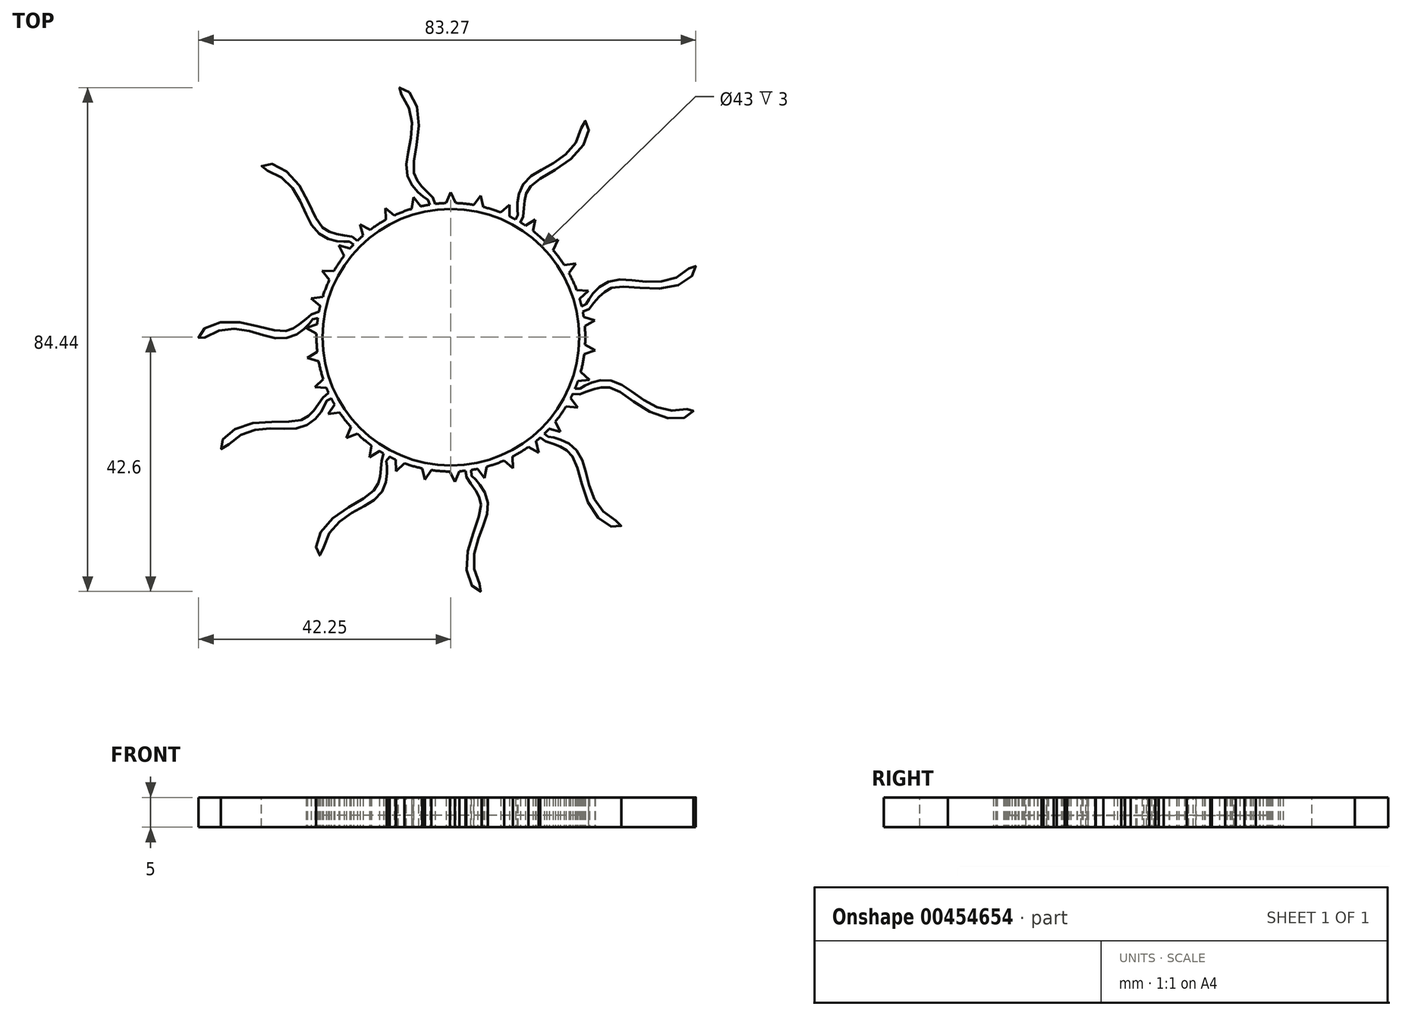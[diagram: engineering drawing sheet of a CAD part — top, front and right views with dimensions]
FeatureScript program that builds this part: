
annotation { "Feature Type Name" : "Feature", "Feature Type Description" : "" }
export const myFeature = defineFeature(function(context is Context, id is Id, definition is map)
    precondition{}
    {
        {
            var Q0;
            Q0=qCreatedBy(makeId("Top.planeOp"),FACE);
            var sketch = newSketch(context, id + "F0", { "sketchPlane" : qUnion([Q0])});
            skCircle(sketch, "E0", {"center": v(0, 0) * mm, "radius": 22.5 * mm});
            skLineSegment(sketch, "E1", {"start": v(-0.8, 22.49) * mm, "end": v(0, 24.26) * mm});
            skLineSegment(sketch, "E2", {"start": v(0, 24.26) * mm, "end": v(0.8, 22.49) * mm});
            skLineSegment(sketch, "E3.1.0", {"start": v(5, 23.74) * mm, "end": v(5.41, 21.84) * mm});
            skLineSegment(sketch, "E3.1.1", {"start": v(3.86, 22.17) * mm, "end": v(5, 23.74) * mm});
            skLineSegment(sketch, "E3.2.0", {"start": v(9.79, 22.2) * mm, "end": v(9.8, 20.25) * mm});
            skLineSegment(sketch, "E3.2.1", {"start": v(8.35, 20.9) * mm, "end": v(9.79, 22.2) * mm});
            skLineSegment(sketch, "E3.3.0", {"start": v(14.16, 19.7) * mm, "end": v(13.76, 17.8) * mm});
            skLineSegment(sketch, "E3.3.1", {"start": v(12.47, 18.73) * mm, "end": v(14.16, 19.7) * mm});
            skLineSegment(sketch, "E3.4.0", {"start": v(17.91, 16.37) * mm, "end": v(17.14, 14.58) * mm});
            skLineSegment(sketch, "E3.4.1", {"start": v(16.07, 15.75) * mm, "end": v(17.91, 16.37) * mm});
            skLineSegment(sketch, "E3.5.0", {"start": v(20.9, 12.32) * mm, "end": v(19.77, 10.73) * mm});
            skLineSegment(sketch, "E3.5.1", {"start": v(18.97, 12.1) * mm, "end": v(20.9, 12.32) * mm});
            skLineSegment(sketch, "E3.6.0", {"start": v(23, 7.75) * mm, "end": v(21.56, 6.43) * mm});
            skLineSegment(sketch, "E3.6.1", {"start": v(21.06, 7.93) * mm, "end": v(23, 7.75) * mm});
            skLineSegment(sketch, "E3.7.0", {"start": v(24.1, 2.84) * mm, "end": v(22.42, 1.85) * mm});
            skLineSegment(sketch, "E3.7.1", {"start": v(22.24, 3.42) * mm, "end": v(24.1, 2.84) * mm});
            skLineSegment(sketch, "E3.8.0", {"start": v(24.17, -2.19) * mm, "end": v(22.32, -2.82) * mm});
            skLineSegment(sketch, "E3.8.1", {"start": v(22.47, -1.24) * mm, "end": v(24.17, -2.19) * mm});
            skLineSegment(sketch, "E3.9.0", {"start": v(23.2, -7.12) * mm, "end": v(21.26, -7.36) * mm});
            skLineSegment(sketch, "E3.9.1", {"start": v(21.73, -5.84) * mm, "end": v(23.2, -7.12) * mm});
            skLineSegment(sketch, "E3.10.0", {"start": v(21.23, -11.75) * mm, "end": v(19.29, -11.58) * mm});
            skLineSegment(sketch, "E3.10.1", {"start": v(20.06, -10.2) * mm, "end": v(21.23, -11.75) * mm});
            skLineSegment(sketch, "E3.11.0", {"start": v(18.35, -15.87) * mm, "end": v(16.49, -15.31) * mm});
            skLineSegment(sketch, "E3.11.1", {"start": v(17.52, -14.11) * mm, "end": v(18.35, -15.87) * mm});
            skLineSegment(sketch, "E3.12.0", {"start": v(14.68, -19.32) * mm, "end": v(12.98, -18.38) * mm});
            skLineSegment(sketch, "E3.12.1", {"start": v(14.24, -17.42) * mm, "end": v(14.68, -19.32) * mm});
            skLineSegment(sketch, "E3.13.0", {"start": v(10.39, -21.93) * mm, "end": v(8.9, -20.66) * mm});
            skLineSegment(sketch, "E3.13.1", {"start": v(10.34, -19.98) * mm, "end": v(10.39, -21.93) * mm});
            skLineSegment(sketch, "E3.14.0", {"start": v(5.64, -23.6) * mm, "end": v(4.46, -22.05) * mm});
            skLineSegment(sketch, "E3.14.1", {"start": v(6, -21.68) * mm, "end": v(5.64, -23.6) * mm});
            skLineSegment(sketch, "E3.15.0", {"start": v(0.66, -24.26) * mm, "end": v(-0.18, -22.5) * mm});
            skLineSegment(sketch, "E3.15.1", {"start": v(1.4, -22.46) * mm, "end": v(0.66, -24.26) * mm});
            skLineSegment(sketch, "E3.16.0", {"start": v(-4.36, -23.87) * mm, "end": v(-4.82, -21.98) * mm});
            skLineSegment(sketch, "E3.16.1", {"start": v(-3.26, -22.26) * mm, "end": v(-4.36, -23.87) * mm});
            skLineSegment(sketch, "E3.17.0", {"start": v(-9.18, -22.46) * mm, "end": v(-9.25, -20.51) * mm});
            skLineSegment(sketch, "E3.17.1", {"start": v(-7.78, -21.11) * mm, "end": v(-9.18, -22.46) * mm});
            skLineSegment(sketch, "E3.18.0", {"start": v(-13.62, -20.08) * mm, "end": v(-13.28, -18.17) * mm});
            skLineSegment(sketch, "E3.18.1", {"start": v(-11.96, -19.06) * mm, "end": v(-13.62, -20.08) * mm});
            skLineSegment(sketch, "E3.19.0", {"start": v(-17.46, -16.84) * mm, "end": v(-16.74, -15.04) * mm});
            skLineSegment(sketch, "E3.19.1", {"start": v(-15.63, -16.18) * mm, "end": v(-17.46, -16.84) * mm});
            skLineSegment(sketch, "E3.20.0", {"start": v(-20.56, -12.88) * mm, "end": v(-19.48, -11.27) * mm});
            skLineSegment(sketch, "E3.20.1", {"start": v(-18.63, -12.61) * mm, "end": v(-20.56, -12.88) * mm});
            skLineSegment(sketch, "E3.21.0", {"start": v(-22.78, -8.37) * mm, "end": v(-21.38, -7) * mm});
            skLineSegment(sketch, "E3.21.1", {"start": v(-20.83, -8.5) * mm, "end": v(-22.78, -8.37) * mm});
            skLineSegment(sketch, "E3.22.0", {"start": v(-24.01, -3.5) * mm, "end": v(-22.37, -2.45) * mm});
            skLineSegment(sketch, "E3.22.1", {"start": v(-22.14, -4.02) * mm, "end": v(-24.01, -3.5) * mm});
            skLineSegment(sketch, "E3.23.0", {"start": v(-24.22, 1.53) * mm, "end": v(-22.4, 2.21) * mm});
            skLineSegment(sketch, "E3.23.1", {"start": v(-22.5, 0.63) * mm, "end": v(-24.22, 1.53) * mm});
            skLineSegment(sketch, "E3.24.0", {"start": v(-23.38, 6.5) * mm, "end": v(-21.45, 6.78) * mm});
            skLineSegment(sketch, "E3.24.1", {"start": v(-21.88, 5.25) * mm, "end": v(-23.38, 6.5) * mm});
            skLineSegment(sketch, "E3.25.0", {"start": v(-21.54, 11.17) * mm, "end": v(-19.6, 11.06) * mm});
            skLineSegment(sketch, "E3.25.1", {"start": v(-20.33, 9.65) * mm, "end": v(-21.54, 11.17) * mm});
            skLineSegment(sketch, "E3.26.0", {"start": v(-18.77, 15.37) * mm, "end": v(-16.9, 14.86) * mm});
            skLineSegment(sketch, "E3.26.1", {"start": v(-17.9, 13.63) * mm, "end": v(-18.77, 15.37) * mm});
            skLineSegment(sketch, "E3.27.0", {"start": v(-15.2, 18.91) * mm, "end": v(-13.47, 18.02) * mm});
            skLineSegment(sketch, "E3.27.1", {"start": v(-14.7, 17.03) * mm, "end": v(-15.2, 18.91) * mm});
            skLineSegment(sketch, "E3.28.0", {"start": v(-10.98, 21.64) * mm, "end": v(-9.46, 20.41) * mm});
            skLineSegment(sketch, "E3.28.1", {"start": v(-10.88, 19.7) * mm, "end": v(-10.98, 21.64) * mm});
            skLineSegment(sketch, "E3.29.0", {"start": v(-6.28, 23.44) * mm, "end": v(-5.05, 21.93) * mm});
            skLineSegment(sketch, "E3.29.1", {"start": v(-6.59, 21.51) * mm, "end": v(-6.28, 23.44) * mm});
            skLineSegment(sketch, "E3.anchor1", {"start": v(0, 0) * mm, "end": v(-0.8, 22.49) * mm, "construction": true});
            skLineSegment(sketch, "E3.anchor2", {"start": v(0, 0) * mm, "end": v(-6.59, 21.51) * mm, "construction": true});
            skFitSpline(sketch, "E4", {"points": [v(-3.54, 22.22) * mm, v(-3.66, 22.83) * mm, v(-3.97, 23.08) * mm, v(-4.5, 23.46) * mm, v(-5.02, 23.84) * mm, v(-5.92, 24.74) * mm, v(-6.9, 26.1) * mm, v(-7.47, 28.4) * mm, v(-7.12, 31.1) * mm, v(-6.52, 35.07) * mm, v(-7.42, 39.32) * mm, v(-8.79, 41.68) * mm, v(-7.6, 41.59) * mm, v(-5.44, 37.44) * mm, v(-6, 30.78) * mm, v(-6.2, 27.57) * mm, v(-5.72, 26.39) * mm, v(-5.12, 25.54) * mm, v(-4.42, 24.8) * mm, v(-3.37, 23.79) * mm, v(-2.87, 23.19) * mm, v(-2.64, 22.34) * mm], "startDerivative": vector(-2.08, 18.4) * mm, "endDerivative": vector(3.18, -21.05) * mm});
            skCircle(sketch, "E5", {"center": v(0, 0) * mm, "radius": 21.5 * mm});
            skFitSpline(sketch, "E6", {"points": [v(10.83, 19.72) * mm, v(11.22, 20.2) * mm, v(11.22, 20.6) * mm, v(11.17, 21.25) * mm, v(11.12, 21.9) * mm, v(11.23, 23.17) * mm, v(11.65, 24.8) * mm, v(13.03, 26.7) * mm, v(15.33, 28.17) * mm, v(18.76, 30.27) * mm, v(21.44, 33.69) * mm, v(22.37, 36.25) * mm, v(23.06, 35.29) * mm, v(21.27, 30.95) * mm, v(15.8, 27.1) * mm, v(13.22, 25.19) * mm, v(12.62, 24.07) * mm, v(12.36, 23.06) * mm, v(12.24, 22.05) * mm, v(12.14, 20.6) * mm, v(12, 19.83) * mm, v(11.5, 19.11) * mm], "startDerivative": vector(12.75, 13.42) * mm, "endDerivative": vector(-14.08, -15.97) * mm});
            skFitSpline(sketch, "E7", {"points": [v(-16.27, 15.54) * mm, v(-16.72, 15.97) * mm, v(-17.12, 16) * mm, v(-17.76, 16) * mm, v(-18.42, 16.02) * mm, v(-19.67, 16.24) * mm, v(-21.25, 16.8) * mm, v(-23.04, 18.34) * mm, v(-24.3, 20.75) * mm, v(-26.09, 24.36) * mm, v(-29.26, 27.33) * mm, v(-31.73, 28.47) * mm, v(-30.71, 29.07) * mm, v(-26.55, 26.92) * mm, v(-23.2, 21.14) * mm, v(-21.51, 18.4) * mm, v(-20.45, 17.7) * mm, v(-19.47, 17.35) * mm, v(-18.47, 17.14) * mm, v(-17.03, 16.92) * mm, v(-16.28, 16.72) * mm, v(-15.6, 16.16) * mm], "startDerivative": vector(-12.26, 13.87) * mm, "endDerivative": vector(14.68, -15.42) * mm});
            skFitSpline(sketch, "E8", {"points": [v(-22.27, 3.18) * mm, v(-22.9, 3.11) * mm, v(-23.22, 2.9) * mm, v(-23.58, 2.47) * mm, v(-24.08, 1.88) * mm, v(-25, 1.03) * mm, v(-26.44, 0.17) * mm, v(-28.77, -0.2) * mm, v(-31.43, 0.39) * mm, v(-35.34, 1.33) * mm, v(-39.65, 0.8) * mm, v(-42.12, -0.35) * mm, v(-41.92, 0.82) * mm, v(-37.6, 2.62) * mm, v(-31.01, 1.47) * mm, v(-27.83, 1) * mm, v(-26.62, 1.37) * mm, v(-25.72, 1.9) * mm, v(-24.91, 2.53) * mm, v(-23.82, 3.49) * mm, v(-23.18, 3.93) * mm, v(-22.08, 4.3) * mm], "startDerivative": vector(-18.5, -0.47) * mm, "endDerivative": vector(21.25, 1.33) * mm});
            skFitSpline(sketch, "E9", {"points": [v(21.9, 5.19) * mm, v(22.5, 5.35) * mm, v(22.72, 5.68) * mm, v(23.05, 6.23) * mm, v(23.38, 6.8) * mm, v(24.2, 7.77) * mm, v(25.47, 8.86) * mm, v(27.7, 9.63) * mm, v(30.43, 9.52) * mm, v(34.44, 9.27) * mm, v(38.6, 10.53) * mm, v(40.83, 12.1) * mm, v(40.84, 10.92) * mm, v(36.89, 8.4) * mm, v(30.2, 8.38) * mm, v(27, 8.28) * mm, v(25.86, 7.71) * mm, v(25.06, 7.04) * mm, v(24.38, 6.28) * mm, v(23.47, 5.14) * mm, v(22.92, 4.6) * mm, v(22.1, 4.26) * mm], "startDerivative": vector(18.14, 3.68) * mm, "endDerivative": vector(-20.7, -5) * mm});
            skFitSpline(sketch, "E10", {"points": [v(-20.03, -10.25) * mm, v(-20.63, -10.47) * mm, v(-20.9, -10.76) * mm, v(-21.12, -11.28) * mm, v(-21.46, -11.97) * mm, v(-22.12, -13.03) * mm, v(-23.3, -14.23) * mm, v(-25.45, -15.2) * mm, v(-28.17, -15.32) * mm, v(-32.2, -15.42) * mm, v(-36.22, -17.04) * mm, v(-38.3, -18.8) * mm, v(-38.42, -17.62) * mm, v(-34.7, -14.76) * mm, v(-28.05, -14.16) * mm, v(-24.86, -13.79) * mm, v(-23.78, -13.12) * mm, v(-23.04, -12.38) * mm, v(-22.43, -11.57) * mm, v(-21.62, -10.35) * mm, v(-21.12, -9.76) * mm, v(-20.16, -9.11) * mm], "startDerivative": vector(-17.75, -5.24) * mm, "endDerivative": vector(20.18, 6.79) * mm});
            skFitSpline(sketch, "E11", {"points": [v(-10.25, -20.03) * mm, v(-10.72, -20.51) * mm, v(-10.8, -20.9) * mm, v(-10.74, -21.45) * mm, v(-10.69, -22.22) * mm, v(-10.73, -23.47) * mm, v(-11.14, -25.1) * mm, v(-12.53, -27) * mm, v(-14.82, -28.48) * mm, v(-18.26, -30.57) * mm, v(-20.94, -34) * mm, v(-21.87, -36.56) * mm, v(-22.55, -35.6) * mm, v(-20.77, -31.26) * mm, v(-15.3, -27.41) * mm, v(-12.72, -25.5) * mm, v(-12.12, -24.38) * mm, v(-11.85, -23.37) * mm, v(-11.73, -22.36) * mm, v(-11.64, -20.9) * mm, v(-11.5, -20.13) * mm, v(-10.99, -19.1) * mm], "startDerivative": vector(-12.75, -13.42) * mm, "endDerivative": vector(14.08, 15.97) * mm});
            skFitSpline(sketch, "E12", {"points": [v(20.7, -8.57) * mm, v(21.3, -8.73) * mm, v(21.66, -8.55) * mm, v(22.22, -8.24) * mm, v(22.8, -7.92) * mm, v(24, -7.49) * mm, v(25.64, -7.18) * mm, v(27.96, -7.62) * mm, v(30.26, -9.08) * mm, v(33.6, -11.3) * mm, v(37.84, -12.3) * mm, v(40.56, -12.05) * mm, v(39.97, -13.08) * mm, v(35.29, -13.3) * mm, v(29.5, -9.96) * mm, v(26.67, -8.44) * mm, v(25.4, -8.36) * mm, v(24.37, -8.55) * mm, v(23.4, -8.87) * mm, v(22.05, -9.4) * mm, v(21.3, -9.6) * mm, v(20.41, -9.47) * mm], "startDerivative": vector(17.55, -5.89) * mm, "endDerivative": vector(-20.43, 6.01) * mm});
            skFitSpline(sketch, "E13", {"points": [v(15.58, -16.04) * mm, v(15.94, -16.55) * mm, v(16.33, -16.64) * mm, v(16.96, -16.77) * mm, v(17.6, -16.89) * mm, v(18.8, -17.32) * mm, v(20.26, -18.14) * mm, v(21.74, -19.98) * mm, v(22.57, -22.57) * mm, v(23.7, -26.43) * mm, v(26.31, -29.9) * mm, v(28.55, -31.47) * mm, v(27.44, -31.88) * mm, v(23.72, -29.03) * mm, v(21.42, -22.76) * mm, v(20.23, -19.77) * mm, v(19.3, -18.9) * mm, v(18.4, -18.38) * mm, v(17.46, -18) * mm, v(16.08, -17.54) * mm, v(15.37, -17.2) * mm, v(14.78, -16.54) * mm], "startDerivative": vector(9.66, -15.8) * mm, "endDerivative": vector(-11.78, 17.74) * mm});
            skFitSpline(sketch, "E14", {"points": [v(3.4, -22.24) * mm, v(3.37, -23.04) * mm, v(3.63, -23.34) * mm, v(4.08, -23.8) * mm, v(4.53, -24.27) * mm, v(5.26, -25.32) * mm, v(5.99, -26.82) * mm, v(6.16, -29.18) * mm, v(5.34, -31.78) * mm, v(4.06, -35.6) * mm, v(4.2, -39.93) * mm, v(5.14, -42.5) * mm, v(4, -42.2) * mm, v(2.58, -37.73) * mm, v(4.3, -31.27) * mm, v(5.04, -28.14) * mm, v(4.78, -26.9) * mm, v(4.34, -25.96) * mm, v(3.78, -25.1) * mm, v(2.92, -23.93) * mm, v(2.53, -23.25) * mm, v(2.42, -22.37) * mm], "startDerivative": vector(-1.15, -18.48) * mm, "endDerivative": vector(0.52, 21.29) * mm});
            skSolve(sketch);
        }
        {
            var Q0;
            Q0 = qSketchRegion(id + "F0", true);
            extrude(context, id + "F1", {"entities" : qUnion([Q0]), "depth" : 5 * mm});
        }
        {
            var Q0;
            Q0=makeQuery(id+"F0.imprint","IMPRINT",FACE,{"disambiguationData":[TD([[makeQuery(id+"F0.imprint","IMPRINT",EDGE,{"derivedFrom":sQuery(id+"F0.wireOp",EDGE,"E5")}),1.0]])]});
            extrude(context, id + "F2", {"entities" : qUnion([Q0]), "operationType" : NewBodyOperationType.ADD, "depth" : 2 * mm});
        }
    });
